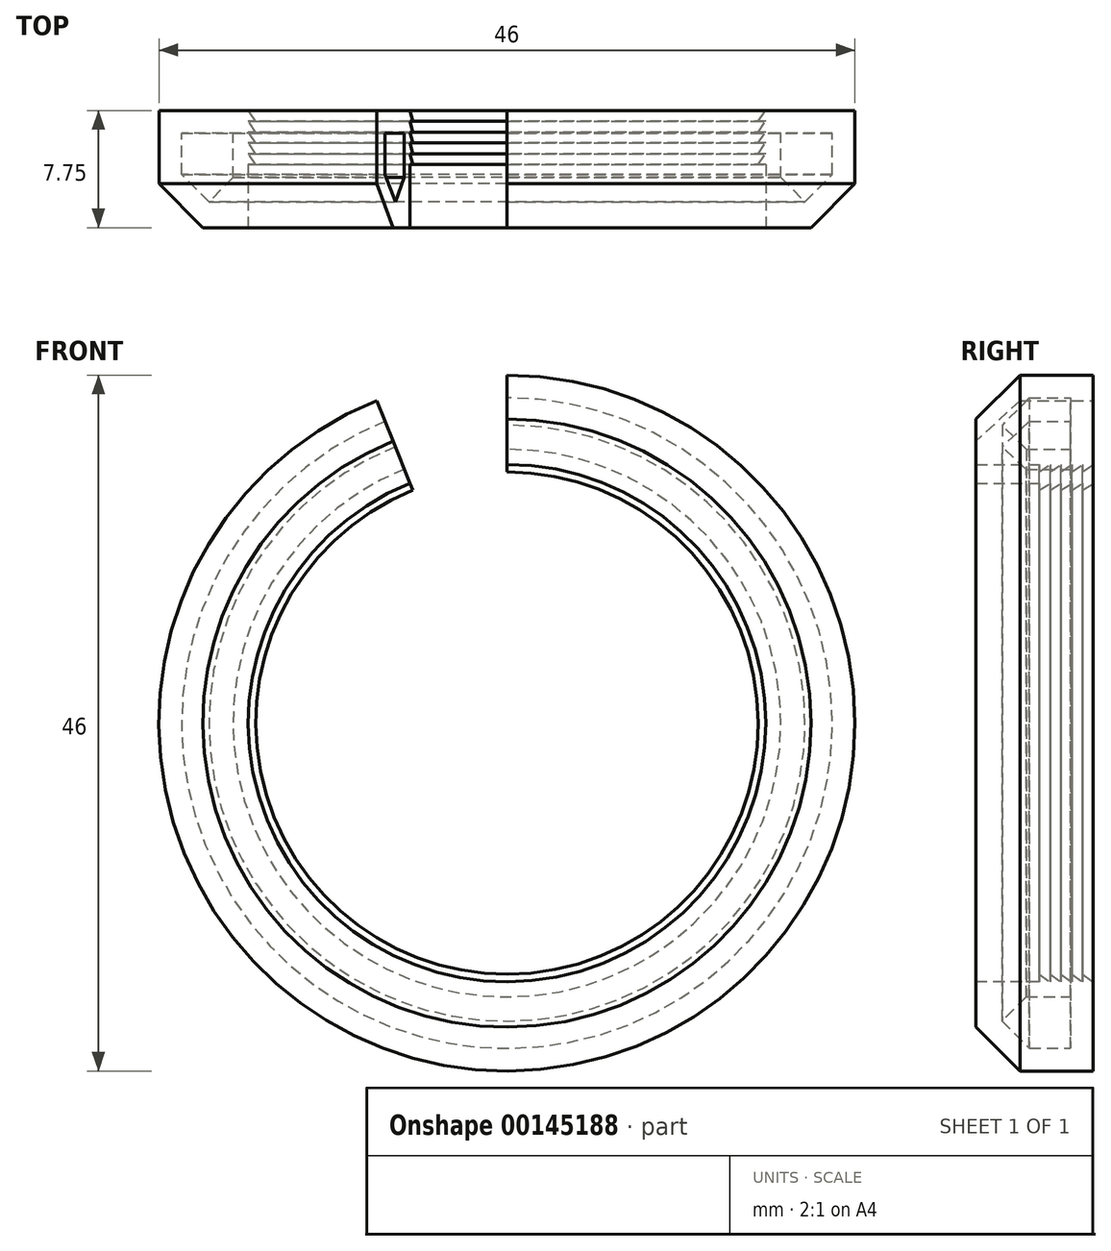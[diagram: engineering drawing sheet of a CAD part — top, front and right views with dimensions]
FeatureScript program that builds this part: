
annotation { "Feature Type Name" : "Feature", "Feature Type Description" : "" }
export const myFeature = defineFeature(function(context is Context, id is Id, definition is map)
    precondition{}
    {
        {
            var Q0;
            Q0=qCreatedBy(makeId("Top.planeOp"),FACE);
            var sketch = newSketch(context, id + "F0", { "sketchPlane" : qUnion([Q0])});
            skLineSegment(sketch, "E0", {"start": v(0, -58.44) * mm, "end": v(0, 42) * mm, "construction": true});
            skSolve(sketch);
        }
        {
            var Q0;
            Q0=qCreatedBy(makeId("Right.planeOp"),FACE);
            var sketch = newSketch(context, id + "F1", { "sketchPlane" : qUnion([Q0])});
            skLineSegment(sketch, "E1", {"start": v(-13.88, 17.1) * mm, "end": v(-13.88, 26.85) * mm});
            skLineSegment(sketch, "E2", {"start": v(-13.88, 26.85) * mm, "end": v(-14.88, 26.85) * mm});
            skLineSegment(sketch, "E3", {"start": v(-14.88, 26.85) * mm, "end": v(-21.63, 20.1) * mm});
            skLineSegment(sketch, "E4", {"start": v(-21.63, 20.1) * mm, "end": v(-21.63, 17.1) * mm});
            skLineSegment(sketch, "E5", {"start": v(-21.63, 17.1) * mm, "end": v(-17.45, 17.1) * mm});
            skLineSegment(sketch, "E6", {"start": v(-17.45, 17.1) * mm, "end": v(-17.45, 16.6) * mm});
            skLineSegment(sketch, "E7", {"start": v(-17.45, 16.6) * mm, "end": v(-16.73, 17.1) * mm});
            skLineSegment(sketch, "E8", {"start": v(-16.73, 17.1) * mm, "end": v(-16.73, 16.6) * mm});
            skLineSegment(sketch, "E9", {"start": v(-16.73, 16.6) * mm, "end": v(-16.02, 17.1) * mm});
            skLineSegment(sketch, "E10", {"start": v(-16.02, 17.1) * mm, "end": v(-16.02, 16.6) * mm});
            skLineSegment(sketch, "E11", {"start": v(-16.02, 16.6) * mm, "end": v(-15.3, 17.1) * mm});
            skLineSegment(sketch, "E12", {"start": v(-15.3, 17.1) * mm, "end": v(-15.3, 16.6) * mm});
            skLineSegment(sketch, "E13", {"start": v(-15.3, 16.6) * mm, "end": v(-14.6, 17.1) * mm});
            skLineSegment(sketch, "E14", {"start": v(-14.6, 17.1) * mm, "end": v(-14.6, 16.6) * mm});
            skLineSegment(sketch, "E15", {"start": v(-14.6, 16.6) * mm, "end": v(-13.88, 17.1) * mm});
            skSolve(sketch);
        }
        {
            var Q0;
            Q0=qSketchRegion(id+"F1",true);
            var Q1;
            Q1=sQuery(id+"F0.wireOp",EDGE,"E0");
            revolve(context, id + "F2", {"entities" : qUnion([Q0]), "axis" : qUnion([Q1]), "revolveType" : RevolveType.ONE_DIRECTION, "angle" : 338 * degree});
        }
        {
            var Q0;
            Q0=qCreatedBy(makeId("Front.planeOp"),FACE);
            var sketch = newSketch(context, id + "F3", { "sketchPlane" : qUnion([Q0])});
            skCircle(sketch, "E16", {"center": v(0, 0) * mm, "radius": 23 * mm});
            skCircle(sketch, "E17", {"center": v(0, 0) * mm, "radius": 43 * mm});
            skSolve(sketch);
        }
        {
            var Q0;
            Q0 = qSketchRegion(id + "F3", true);
            extrude(context, id + "F4", {"entities" : qUnion([Q0]), "operationType" : NewBodyOperationType.REMOVE, "depth" : 25 * mm});
        }
        {
            var Q0;
            Q0=makeQuery(id+"F2.opRevolve","CAP_FACE",FACE,{"disambiguationData":[OSD([sQuery(id+"F1.wireOp",EDGE,"E1"),sQuery(id+"F1.wireOp",EDGE,"E2"),sQuery(id+"F1.wireOp",EDGE,"E3"),sQuery(id+"F1.wireOp",EDGE,"E4"),sQuery(id+"F1.wireOp",EDGE,"E5"),sQuery(id+"F1.wireOp",EDGE,"E6"),sQuery(id+"F1.wireOp",EDGE,"E7"),sQuery(id+"F1.wireOp",EDGE,"E8"),sQuery(id+"F1.wireOp",EDGE,"E9"),sQuery(id+"F1.wireOp",EDGE,"E10"),sQuery(id+"F1.wireOp",EDGE,"E11"),sQuery(id+"F1.wireOp",EDGE,"E12"),sQuery(id+"F1.wireOp",EDGE,"E13"),sQuery(id+"F1.wireOp",EDGE,"E14"),sQuery(id+"F1.wireOp",EDGE,"E15")])],"isStart":false});
            var sketch = newSketch(context, id + "F5", { "sketchPlane" : qUnion([Q0])});
            skLineSegment(sketch, "E18", {"start": v(-15.38, 21.5) * mm, "end": v(-18.1, 21.5) * mm});
            skLineSegment(sketch, "E19", {"start": v(-18.1, 21.5) * mm, "end": v(-19.91, 19.7) * mm});
            skLineSegment(sketch, "E20", {"start": v(-19.91, 19.7) * mm, "end": v(-18.31, 18.1) * mm});
            skLineSegment(sketch, "E21", {"start": v(-18.31, 18.1) * mm, "end": v(-15.38, 18.1) * mm});
            skLineSegment(sketch, "E22", {"start": v(-15.38, 18.1) * mm, "end": v(-15.38, 21.5) * mm});
            skSolve(sketch);
        }
        {
            var Q0;
            Q0 = qSketchRegion(id + "F5", true);
            var Q1;
            Q1=sQuery(id+"F0.wireOp",EDGE,"E0");
            revolve(context, id + "F6", {"operationType" : NewBodyOperationType.REMOVE, "entities" : qUnion([Q0]), "axis" : qUnion([Q1]), "revolveType" : RevolveType.FULL, "oppositeDirection" : true});
        }
    });
